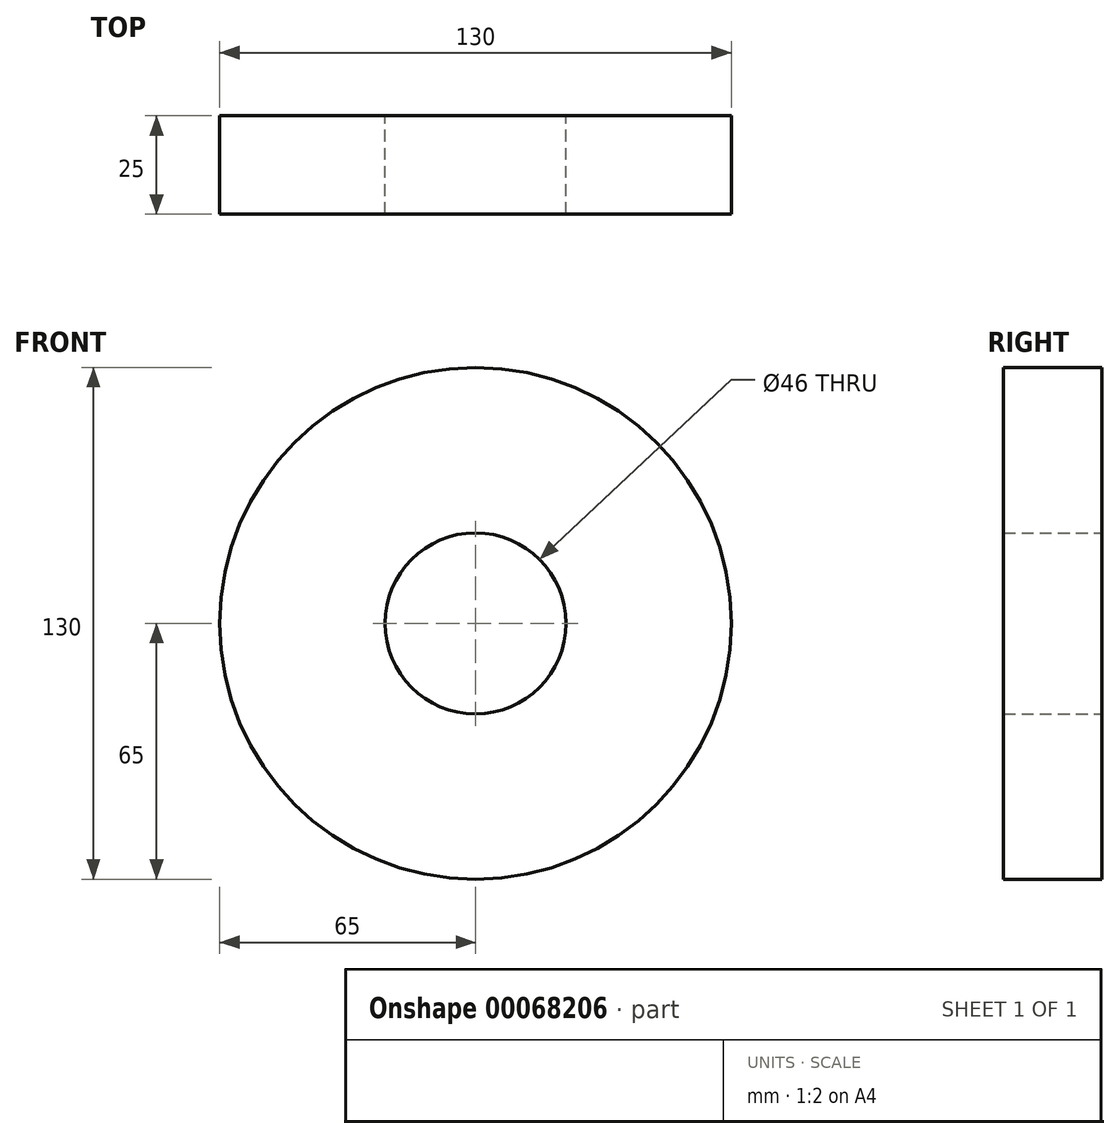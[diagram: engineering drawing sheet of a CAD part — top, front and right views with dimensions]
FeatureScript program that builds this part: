
annotation { "Feature Type Name" : "Feature", "Feature Type Description" : "" }
export const myFeature = defineFeature(function(context is Context, id is Id, definition is map)
    precondition{}
    {
        {
            var Q0;
            Q0=qCreatedBy(makeId("Front.planeOp"),FACE);
            var sketch = newSketch(context, id + "F0", { "sketchPlane" : qUnion([Q0])});
            skCircle(sketch, "E0", {"center": v(0, 0) * mm, "radius": 65 * mm});
            skCircle(sketch, "E1", {"center": v(0, 0) * mm, "radius": 23 * mm});
            skSolve(sketch);
        }
        {
            var Q0;
            Q0=makeQuery(id+"F0.imprint","IMPRINT",FACE,{"disambiguationData":[TD([[makeQuery(id+"F0.imprint","IMPRINT",EDGE,{"derivedFrom":sQuery(id+"F0.wireOp",EDGE,"E0")}),1.0]])]});
            extrude(context, id + "F1", {"entities" : qUnion([Q0]), "depth" : 25 * mm});
        }
    });
